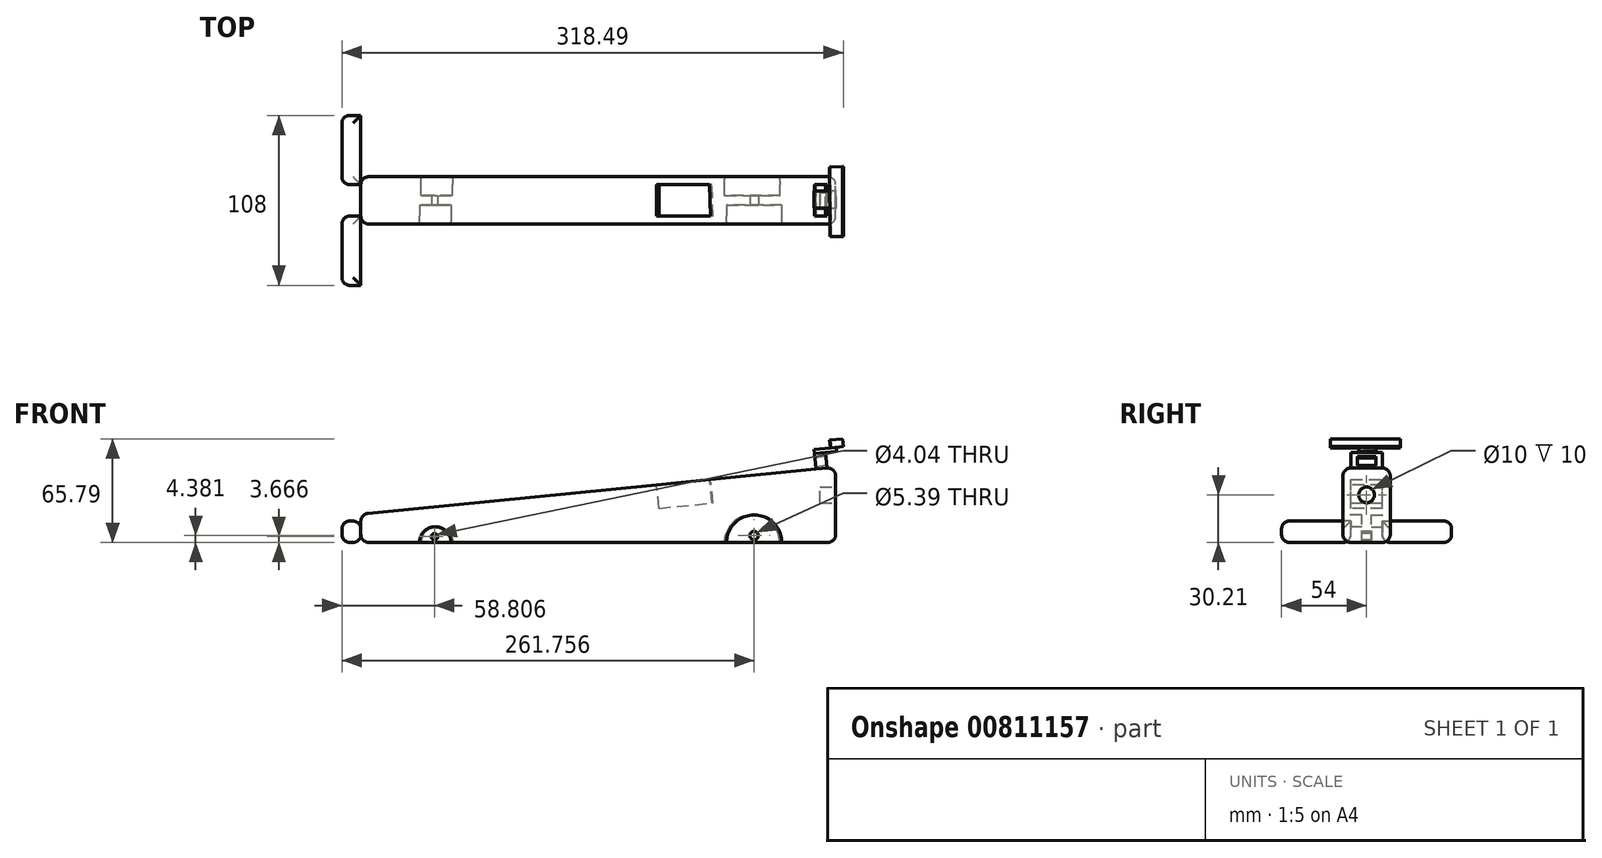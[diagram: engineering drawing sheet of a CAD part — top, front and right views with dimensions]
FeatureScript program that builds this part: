
annotation { "Feature Type Name" : "Feature", "Feature Type Description" : "" }
export const myFeature = defineFeature(function(context is Context, id is Id, definition is map)
    precondition{}
    {
        {
            var Q0;
            Q0=qCreatedBy(makeId("Front.planeOp"),FACE);
            var sketch = newSketch(context, id + "F0", { "sketchPlane" : qUnion([Q0])});
            skLineSegment(sketch, "E0", {"start": v(-158.15, -36.12) * mm, "end": v(143.47, -36.12) * mm});
            skLineSegment(sketch, "E1", {"start": v(143.47, -36.12) * mm, "end": v(143.47, 11.66) * mm});
            skLineSegment(sketch, "E2", {"start": v(-158.15, -36.12) * mm, "end": v(-158.15, -17.99) * mm});
            skLineSegment(sketch, "E3", {"start": v(-158.15, -17.99) * mm, "end": v(143.47, 11.66) * mm});
            skSolve(sketch);
        }
        {
            var Q0;
            Q0 = qSketchRegion(id + "F0", true);
            extrude(context, id + "F1", {"entities" : qUnion([Q0]), "depth" : 30 * mm, "offsetDistance" : 25 * mm});
        }
        {
            var Q0;
            Q0=makeQuery(id+"F1.opExtrude","CAP_FACE",FACE,{"disambiguationData":[OSD([sQuery(id+"F0.wireOp",EDGE,"E0"),sQuery(id+"F0.wireOp",EDGE,"E1"),sQuery(id+"F0.wireOp",EDGE,"E2"),sQuery(id+"F0.wireOp",EDGE,"E3")])],"isStart":false});
            var sketch = newSketch(context, id + "F2", { "sketchPlane" : qUnion([Q0])});
            skCircle(sketch, "E4", {"center": v(-110.88, -36.12) * mm, "radius": 10 * mm});
            skCircle(sketch, "E5", {"center": v(91.67, -36.12) * mm, "radius": 17.5 * mm});
            skSolve(sketch);
        }
        {
            var Q0;
            Q0 = qSketchRegion(id + "F2", true);
            extrude(context, id + "F3", {"entities" : qUnion([Q0]), "operationType" : NewBodyOperationType.REMOVE, "oppositeDirection" : true, "depth" : 12 * mm, "offsetDistance" : 25 * mm});
        }
        {
            var Q0;
            Q0=makeQuery(id+"F1.opExtrude","CAP_FACE",FACE,{"disambiguationData":[OSD([sQuery(id+"F0.wireOp",EDGE,"E0"),sQuery(id+"F0.wireOp",EDGE,"E1"),sQuery(id+"F0.wireOp",EDGE,"E2"),sQuery(id+"F0.wireOp",EDGE,"E3")])],"isStart":true});
            var sketch = newSketch(context, id + "F4", { "sketchPlane" : qUnion([Q0])});
            skCircle(sketch, "E6", {"center": v(109.85, -36.12) * mm, "radius": 10 * mm});
            skCircle(sketch, "E7", {"center": v(-90.42, -36.12) * mm, "radius": 17.5 * mm});
            skSolve(sketch);
        }
        {
            var Q0;
            Q0 = qSketchRegion(id + "F4", true);
            extrude(context, id + "F5", {"entities" : qUnion([Q0]), "operationType" : NewBodyOperationType.REMOVE, "oppositeDirection" : true, "depth" : 12 * mm, "offsetDistance" : 25 * mm});
        }
        {
            var Q0;
            Q0=makeQuery(id+"F1.opExtrude","SWEPT_EDGE",EDGE,{"disambiguationData":[OSD([sQuery(id+"F0.wireOp",EDGE,"E2"),sQuery(id+"F0.wireOp",EDGE,"E3")])]});
            var Q1;
            Q1=makeQuery(id+"F1.opExtrude","CAP_EDGE",EDGE,{"disambiguationData":[OSD([sQuery(id+"F0.wireOp",EDGE,"E3")])],"isStart":false});
            var Q2;
            Q2=makeQuery(id+"F3.boolean.opBoolean","COPY",EDGE,{"derivedFrom":makeQuery(id+"F3.opExtrude","CAP_EDGE",EDGE,{"disambiguationData":[OSD([sQuery(id+"F2.wireOp",EDGE,"E4")])],"isStart":true})});
            var Q3;
            Q3=makeQuery(id+"F1.opExtrude","CAP_EDGE",EDGE,{"disambiguationData":[OSD([sQuery(id+"F0.wireOp",EDGE,"E2")])],"isStart":false});
            var Q4;
            Q4=makeQuery(id+"F3.boolean.opBoolean","COPY",EDGE,{"derivedFrom":makeQuery(id+"F3.opExtrude","CAP_EDGE",EDGE,{"disambiguationData":[OSD([sQuery(id+"F2.wireOp",EDGE,"E5")])],"isStart":true})});
            var Q5;
            Q5=makeQuery(id+"F1.opExtrude","CAP_EDGE",EDGE,{"disambiguationData":[OSD([sQuery(id+"F0.wireOp",EDGE,"E2")])],"isStart":true});
            var Q6;
            Q6=makeQuery(id+"F5.boolean.opBoolean","COPY",EDGE,{"derivedFrom":makeQuery(id+"F5.opExtrude","CAP_EDGE",EDGE,{"disambiguationData":[OSD([sQuery(id+"F4.wireOp",EDGE,"E6")])],"isStart":true})});
            var Q7;
            Q7=makeQuery(id+"F5.boolean.opBoolean","COPY",EDGE,{"derivedFrom":makeQuery(id+"F5.opExtrude","CAP_EDGE",EDGE,{"disambiguationData":[OSD([sQuery(id+"F4.wireOp",EDGE,"E7")])],"isStart":true})});
            var Q8;
            Q8=makeQuery(id+"F1.opExtrude","CAP_EDGE",EDGE,{"disambiguationData":[OSD([sQuery(id+"F0.wireOp",EDGE,"E3")])],"isStart":true});
            var Q9;
            Q9=makeQuery(id+"F1.opExtrude","CAP_EDGE",EDGE,{"disambiguationData":[OSD([sQuery(id+"F0.wireOp",EDGE,"E1")])],"isStart":true});
            var Q10;
            Q10=makeQuery(id+"F1.opExtrude","CAP_EDGE",EDGE,{"disambiguationData":[OSD([sQuery(id+"F0.wireOp",EDGE,"E1")])],"isStart":false});
            var Q11;
            Q11=makeQuery(id+"F1.opExtrude","SWEPT_EDGE",EDGE,{"disambiguationData":[OSD([sQuery(id+"F0.wireOp",EDGE,"E1"),sQuery(id+"F0.wireOp",EDGE,"E3")])]});
            var Q12;
            {var subQ0=sQuery(id+"F0.wireOp",EDGE,"E0");Q12=makeQuery(id+"F5.boolean.opBoolean","SPLIT",EDGE,{"disambiguationData":[TD([makeQuery(id+"F1.opExtrude","SWEPT_FACE",FACE,{"disambiguationData":[OSD([subQ0])]}),makeQuery(id+"F1.opExtrude","CAP_FACE",FACE,{"disambiguationData":[OSD([subQ0,sQuery(id+"F0.wireOp",EDGE,"E1"),sQuery(id+"F0.wireOp",EDGE,"E2"),sQuery(id+"F0.wireOp",EDGE,"E3")])],"isStart":true}),makeQuery(id+"F5.opExtrude","SWEPT_FACE",FACE,{"disambiguationData":[OSD([sQuery(id+"F4.wireOp",EDGE,"E6")])]}),makeQuery(id+"F5.opExtrude","SWEPT_FACE",FACE,{"disambiguationData":[OSD([sQuery(id+"F4.wireOp",EDGE,"E7")])]})])],"derivedFrom":makeQuery(id+"F1.opExtrude","CAP_EDGE",EDGE,{"disambiguationData":[OSD([subQ0])],"isStart":true})});}
            var Q13;
            {var subQ0=sQuery(id+"F0.wireOp",EDGE,"E0");Q13=makeQuery(id+"F3.boolean.opBoolean","SPLIT",EDGE,{"disambiguationData":[TD([makeQuery(id+"F1.opExtrude","SWEPT_FACE",FACE,{"disambiguationData":[OSD([subQ0])]}),makeQuery(id+"F1.opExtrude","CAP_FACE",FACE,{"disambiguationData":[OSD([subQ0,sQuery(id+"F0.wireOp",EDGE,"E1"),sQuery(id+"F0.wireOp",EDGE,"E2"),sQuery(id+"F0.wireOp",EDGE,"E3")])],"isStart":false}),makeQuery(id+"F3.opExtrude","SWEPT_FACE",FACE,{"disambiguationData":[OSD([sQuery(id+"F2.wireOp",EDGE,"E4")])]}),makeQuery(id+"F3.opExtrude","SWEPT_FACE",FACE,{"disambiguationData":[OSD([sQuery(id+"F2.wireOp",EDGE,"E5")])]})])],"derivedFrom":makeQuery(id+"F1.opExtrude","CAP_EDGE",EDGE,{"disambiguationData":[OSD([subQ0])],"isStart":false})});}
            var Q14;
            {var subQ0=sQuery(id+"F0.wireOp",EDGE,"E0");var subQ1=sQuery(id+"F0.wireOp",EDGE,"E1");Q14=makeQuery(id+"F3.boolean.opBoolean","SPLIT",EDGE,{"disambiguationData":[TD([makeQuery(id+"F1.opExtrude","SWEPT_FACE",FACE,{"disambiguationData":[OSD([subQ0])]}),makeQuery(id+"F1.opExtrude","CAP_FACE",FACE,{"disambiguationData":[OSD([subQ0,subQ1,sQuery(id+"F0.wireOp",EDGE,"E2"),sQuery(id+"F0.wireOp",EDGE,"E3")])],"isStart":false}),makeQuery(id+"F1.opExtrude","SWEPT_FACE",FACE,{"disambiguationData":[OSD([subQ1])]}),makeQuery(id+"F3.opExtrude","SWEPT_FACE",FACE,{"disambiguationData":[OSD([sQuery(id+"F2.wireOp",EDGE,"E5")])]})])],"derivedFrom":makeQuery(id+"F1.opExtrude","CAP_EDGE",EDGE,{"disambiguationData":[OSD([subQ0])],"isStart":false})});}
            var Q15;
            {var subQ0=sQuery(id+"F0.wireOp",EDGE,"E0");var subQ1=sQuery(id+"F0.wireOp",EDGE,"E1");Q15=makeQuery(id+"F5.boolean.opBoolean","SPLIT",EDGE,{"disambiguationData":[TD([makeQuery(id+"F1.opExtrude","SWEPT_FACE",FACE,{"disambiguationData":[OSD([subQ0])]}),makeQuery(id+"F1.opExtrude","CAP_FACE",FACE,{"disambiguationData":[OSD([subQ0,subQ1,sQuery(id+"F0.wireOp",EDGE,"E2"),sQuery(id+"F0.wireOp",EDGE,"E3")])],"isStart":true}),makeQuery(id+"F1.opExtrude","SWEPT_FACE",FACE,{"disambiguationData":[OSD([subQ1])]}),makeQuery(id+"F5.opExtrude","SWEPT_FACE",FACE,{"disambiguationData":[OSD([sQuery(id+"F4.wireOp",EDGE,"E7")])]})])],"derivedFrom":makeQuery(id+"F1.opExtrude","CAP_EDGE",EDGE,{"disambiguationData":[OSD([subQ0])],"isStart":true})});}
            var Q16;
            {var subQ0=sQuery(id+"F0.wireOp",EDGE,"E0");var subQ1=sQuery(id+"F0.wireOp",EDGE,"E2");Q16=makeQuery(id+"F5.boolean.opBoolean","SPLIT",EDGE,{"disambiguationData":[TD([makeQuery(id+"F1.opExtrude","SWEPT_FACE",FACE,{"disambiguationData":[OSD([subQ0])]}),makeQuery(id+"F1.opExtrude","CAP_FACE",FACE,{"disambiguationData":[OSD([subQ0,sQuery(id+"F0.wireOp",EDGE,"E1"),subQ1,sQuery(id+"F0.wireOp",EDGE,"E3")])],"isStart":true}),makeQuery(id+"F1.opExtrude","SWEPT_FACE",FACE,{"disambiguationData":[OSD([subQ1])]}),makeQuery(id+"F5.opExtrude","SWEPT_FACE",FACE,{"disambiguationData":[OSD([sQuery(id+"F4.wireOp",EDGE,"E6")])]})])],"derivedFrom":makeQuery(id+"F1.opExtrude","CAP_EDGE",EDGE,{"disambiguationData":[OSD([subQ0])],"isStart":true})});}
            var Q17;
            {var subQ0=sQuery(id+"F0.wireOp",EDGE,"E0");var subQ1=sQuery(id+"F0.wireOp",EDGE,"E2");Q17=makeQuery(id+"F3.boolean.opBoolean","SPLIT",EDGE,{"disambiguationData":[TD([makeQuery(id+"F1.opExtrude","SWEPT_FACE",FACE,{"disambiguationData":[OSD([subQ0])]}),makeQuery(id+"F1.opExtrude","CAP_FACE",FACE,{"disambiguationData":[OSD([subQ0,sQuery(id+"F0.wireOp",EDGE,"E1"),subQ1,sQuery(id+"F0.wireOp",EDGE,"E3")])],"isStart":false}),makeQuery(id+"F1.opExtrude","SWEPT_FACE",FACE,{"disambiguationData":[OSD([subQ1])]}),makeQuery(id+"F3.opExtrude","SWEPT_FACE",FACE,{"disambiguationData":[OSD([sQuery(id+"F2.wireOp",EDGE,"E4")])]})])],"derivedFrom":makeQuery(id+"F1.opExtrude","CAP_EDGE",EDGE,{"disambiguationData":[OSD([subQ0])],"isStart":false})});}
            var Q18;
            Q18=makeQuery(id+"F1.opExtrude","SWEPT_EDGE",EDGE,{"disambiguationData":[OSD([sQuery(id+"F0.wireOp",EDGE,"E0"),sQuery(id+"F0.wireOp",EDGE,"E1")])]});
            fillet(context, id + "F6", {"entities" : qUnion([Q0, Q1, Q2, Q3, Q4, Q5, Q6, Q7, Q8, Q9, Q10, Q11, Q12, Q13, Q14, Q15, Q16, Q17, Q18]), "radius" : 5 * mm, "tangentPropagation" : true, "allowEdgeOverflow" : false});
        }
        {
            var Q0;
            Q0=makeQuery(id+"F1.opExtrude","SWEPT_FACE",FACE,{"disambiguationData":[OSD([sQuery(id+"F0.wireOp",EDGE,"E3")])]});
            var sketch = newSketch(context, id + "F7", { "sketchPlane" : qUnion([Q0])});
            skLineSegment(sketch, "E8", {"start": v(131.22, -5) * mm, "end": v(131.22, -25) * mm});
            skLineSegment(sketch, "E9", {"start": v(131.22, -25) * mm, "end": v(138.4, -25) * mm});
            skLineSegment(sketch, "E10", {"start": v(138.4, -25) * mm, "end": v(138.4, -5) * mm});
            skLineSegment(sketch, "E11", {"start": v(138.4, -5) * mm, "end": v(131.22, -5) * mm});
            skSolve(sketch);
        }
        {
            var Q0;
            Q0 = qSketchRegion(id + "F7", true);
            extrude(context, id + "F8", {"entities" : qUnion([Q0]), "operationType" : NewBodyOperationType.ADD, "depth" : 10 * mm, "offsetDistance" : 25 * mm});
        }
        {
            var Q0;
            Q0=makeQuery(id+"F8.opExtrude","CAP_FACE",FACE,{"disambiguationData":[OSD([sQuery(id+"F7.wireOp",EDGE,"E8"),sQuery(id+"F7.wireOp",EDGE,"E9"),sQuery(id+"F7.wireOp",EDGE,"E10"),sQuery(id+"F7.wireOp",EDGE,"E11")])],"isStart":false});
            var sketch = newSketch(context, id + "F9", { "sketchPlane" : qUnion([Q0])});
            skLineSegment(sketch, "E12", {"start": v(131.22, -9.22) * mm, "end": v(131.22, -20) * mm});
            skLineSegment(sketch, "E13", {"start": v(131.22, -20) * mm, "end": v(145.56, -20) * mm});
            skLineSegment(sketch, "E14", {"start": v(145.56, -20) * mm, "end": v(145.56, -9.13) * mm});
            skLineSegment(sketch, "E15", {"start": v(145.56, -9.13) * mm, "end": v(131.22, -9.22) * mm});
            skSolve(sketch);
        }
        {
            var Q0;
            Q0 = qSketchRegion(id + "F9", true);
            extrude(context, id + "F10", {"entities" : qUnion([Q0]), "operationType" : NewBodyOperationType.ADD, "depth" : 2.5 * mm, "offsetDistance" : 25 * mm});
        }
        {
            var Q0;
            Q0=makeQuery(id+"F10.opExtrude","CAP_FACE",FACE,{"disambiguationData":[OSD([sQuery(id+"F9.wireOp",EDGE,"E12"),sQuery(id+"F9.wireOp",EDGE,"E13"),sQuery(id+"F9.wireOp",EDGE,"E14"),sQuery(id+"F9.wireOp",EDGE,"E15")])],"isStart":false});
            var sketch = newSketch(context, id + "F11", { "sketchPlane" : qUnion([Q0])});
            skLineSegment(sketch, "E16", {"start": v(141.8, 6.32) * mm, "end": v(142.05, -37.95) * mm});
            skPoint(sketch, "E17.start.orphan", {"position": v(151.86, 7.12) * mm});
            skLineSegment(sketch, "E18", {"start": v(141.8, 6.32) * mm, "end": v(150.04, 6.37) * mm});
            skLineSegment(sketch, "E19", {"start": v(150.04, 6.37) * mm, "end": v(150.04, -37.9) * mm});
            skPoint(sketch, "E20.end.orphan", {"position": v(151.86, -37.9) * mm});
            skLineSegment(sketch, "E21", {"start": v(142.05, -37.95) * mm, "end": v(150.04, -37.9) * mm});
            skSolve(sketch);
        }
        {
            var Q0;
            Q0 = qSketchRegion(id + "F11", true);
            extrude(context, id + "F12", {"entities" : qUnion([Q0]), "operationType" : NewBodyOperationType.ADD, "depth" : 5 * mm, "offsetDistance" : 25 * mm});
        }
        {
            var Q0;
            Q0=makeQuery(id+"F10.boolean.opBoolean","MERGE",FACE,{"derivedFrom":[makeQuery(id+"F8.opExtrude","SWEPT_FACE",FACE,{"disambiguationData":[OSD([sQuery(id+"F7.wireOp",EDGE,"E8")])]}),makeQuery(id+"F10.opExtrude","SWEPT_FACE",FACE,{"disambiguationData":[OSD([sQuery(id+"F9.wireOp",EDGE,"E12")])]})]});
            var sketch = newSketch(context, id + "F13", { "sketchPlane" : qUnion([Q0])});
            skLineSegment(sketch, "E22.bottom", {"start": v(9.22, 4.84) * mm, "end": v(20.97, 4.84) * mm});
            skLineSegment(sketch, "E22.top", {"start": v(9.22, -0.9) * mm, "end": v(20.97, -0.9) * mm});
            skLineSegment(sketch, "E22.left", {"start": v(9.22, 4.84) * mm, "end": v(9.22, -0.9) * mm});
            skLineSegment(sketch, "E22.right", {"start": v(20.97, 4.84) * mm, "end": v(20.97, -0.9) * mm});
            skSolve(sketch);
        }
        {
            var Q0;
            Q0 = qSketchRegion(id + "F13", true);
            extrude(context, id + "F14", {"entities" : qUnion([Q0]), "operationType" : NewBodyOperationType.REMOVE, "oppositeDirection" : true, "depth" : 25 * mm, "offsetDistance" : 25 * mm});
        }
        {
            var Q0;
            Q0=makeQuery(id+"F3.boolean.opBoolean","COPY",FACE,{"derivedFrom":makeQuery(id+"F3.opExtrude","CAP_FACE",FACE,{"disambiguationData":[OSD([sQuery(id+"F2.wireOp",EDGE,"E4")])],"isStart":false})});
            var sketch = newSketch(context, id + "F15", { "sketchPlane" : qUnion([Q0])});
            skCircle(sketch, "E23", {"center": v(-111.34, -32.45) * mm, "radius": 2.02 * mm});
            skSolve(sketch);
        }
        {
            var Q0;
            Q0 = qSketchRegion(id + "F15", true);
            extrude(context, id + "F16", {"entities" : qUnion([Q0]), "operationType" : NewBodyOperationType.REMOVE, "oppositeDirection" : true, "depth" : 25 * mm, "offsetDistance" : 25 * mm});
        }
        {
            var Q0;
            Q0=makeQuery(id+"F3.boolean.opBoolean","COPY",FACE,{"derivedFrom":makeQuery(id+"F3.opExtrude","CAP_FACE",FACE,{"disambiguationData":[OSD([sQuery(id+"F2.wireOp",EDGE,"E5")])],"isStart":false})});
            var sketch = newSketch(context, id + "F17", { "sketchPlane" : qUnion([Q0])});
            skCircle(sketch, "E24", {"center": v(91.6, -31.74) * mm, "radius": 2.7 * mm});
            skSolve(sketch);
        }
        {
            var Q0;
            Q0 = qSketchRegion(id + "F17", true);
            extrude(context, id + "F18", {"entities" : qUnion([Q0]), "operationType" : NewBodyOperationType.REMOVE, "oppositeDirection" : true, "depth" : 25 * mm, "offsetDistance" : 25 * mm});
        }
        {
            var Q0;
            Q0=makeQuery(id+"F1.opExtrude","SWEPT_FACE",FACE,{"disambiguationData":[OSD([sQuery(id+"F0.wireOp",EDGE,"E2")])]});
            var sketch = newSketch(context, id + "F19", { "sketchPlane" : qUnion([Q0])});
            skLineSegment(sketch, "E25", {"start": v(5, -22.52) * mm, "end": v(-39, -22.52) * mm});
            skLineSegment(sketch, "E26", {"start": v(-39, -22.52) * mm, "end": v(-39, -36.12) * mm});
            skLineSegment(sketch, "E27", {"start": v(-39, -36.12) * mm, "end": v(5, -36.12) * mm});
            skLineSegment(sketch, "E28", {"start": v(5, -36.12) * mm, "end": v(5, -22.52) * mm});
            skLineSegment(sketch, "E29", {"start": v(25, -22.52) * mm, "end": v(69, -22.52) * mm});
            skLineSegment(sketch, "E30", {"start": v(69, -22.52) * mm, "end": v(69, -36.12) * mm});
            skLineSegment(sketch, "E31", {"start": v(69, -36.12) * mm, "end": v(25, -36.12) * mm});
            skLineSegment(sketch, "E32", {"start": v(25, -36.12) * mm, "end": v(25, -22.52) * mm});
            skSolve(sketch);
        }
        {
            var Q0;
            Q0 = qSketchRegion(id + "F19", true);
            extrude(context, id + "F20", {"entities" : qUnion([Q0]), "depth" : 12 * mm, "offsetDistance" : 25 * mm});
        }
        {
            var Q0;
            Q0=makeQuery(id+"F20.opExtrude","CAP_EDGE",EDGE,{"disambiguationData":[OSD([sQuery(id+"F19.wireOp",EDGE,"E25")])],"isStart":false});
            var Q1;
            Q1=makeQuery(id+"F20.opExtrude","CAP_EDGE",EDGE,{"disambiguationData":[OSD([sQuery(id+"F19.wireOp",EDGE,"E29")])],"isStart":false});
            var Q2;
            Q2=makeQuery(id+"F20.opExtrude","CAP_EDGE",EDGE,{"disambiguationData":[OSD([sQuery(id+"F19.wireOp",EDGE,"E30")])],"isStart":false});
            var Q3;
            Q3=makeQuery(id+"F20.opExtrude","CAP_EDGE",EDGE,{"disambiguationData":[OSD([sQuery(id+"F19.wireOp",EDGE,"E31")])],"isStart":false});
            var Q4;
            Q4=makeQuery(id+"F20.opExtrude","CAP_EDGE",EDGE,{"disambiguationData":[OSD([sQuery(id+"F19.wireOp",EDGE,"E27")])],"isStart":false});
            var Q5;
            Q5=makeQuery(id+"F20.opExtrude","CAP_EDGE",EDGE,{"disambiguationData":[OSD([sQuery(id+"F19.wireOp",EDGE,"E26")])],"isStart":false});
            var Q6;
            Q6=makeQuery(id+"F20.opExtrude","SWEPT_EDGE",EDGE,{"disambiguationData":[OSD([sQuery(id+"F19.wireOp",EDGE,"E30"),sQuery(id+"F19.wireOp",EDGE,"E31")])]});
            var Q7;
            Q7=makeQuery(id+"F20.opExtrude","SWEPT_EDGE",EDGE,{"disambiguationData":[OSD([sQuery(id+"F19.wireOp",EDGE,"E29"),sQuery(id+"F19.wireOp",EDGE,"E30")])]});
            var Q8;
            Q8=makeQuery(id+"F20.opExtrude","CAP_EDGE",EDGE,{"disambiguationData":[OSD([sQuery(id+"F19.wireOp",EDGE,"E28")])],"isStart":false});
            var Q9;
            Q9=makeQuery(id+"F20.opExtrude","CAP_EDGE",EDGE,{"disambiguationData":[OSD([sQuery(id+"F19.wireOp",EDGE,"E32")])],"isStart":false});
            var Q10;
            Q10=makeQuery(id+"F20.opExtrude","SWEPT_EDGE",EDGE,{"disambiguationData":[OSD([sQuery(id+"F19.wireOp",EDGE,"E25"),sQuery(id+"F19.wireOp",EDGE,"E26")])]});
            var Q11;
            Q11=makeQuery(id+"F20.opExtrude","SWEPT_EDGE",EDGE,{"disambiguationData":[OSD([sQuery(id+"F19.wireOp",EDGE,"E26"),sQuery(id+"F19.wireOp",EDGE,"E27")])]});
            var Q12;
            Q12=makeQuery(id+"F20.opExtrude","CAP_EDGE",EDGE,{"disambiguationData":[OSD([sQuery(id+"F19.wireOp",EDGE,"E31")])],"isStart":true});
            var Q13;
            Q13=makeQuery(id+"F20.opExtrude","CAP_EDGE",EDGE,{"disambiguationData":[OSD([sQuery(id+"F19.wireOp",EDGE,"E27")])],"isStart":true});
            var Q14;
            Q14=makeQuery(id+"F20.opExtrude","SWEPT_EDGE",EDGE,{"disambiguationData":[OSD([sQuery(id+"F0.wireOp",EDGE,"E0"),sQuery(id+"F0.wireOp",EDGE,"E2"),sQuery(id+"F19.wireOp",EDGE,"E27"),sQuery(id+"F19.wireOp",EDGE,"E28")])]});
            var Q15;
            Q15=makeQuery(id+"F20.opExtrude","SWEPT_EDGE",EDGE,{"disambiguationData":[OSD([sQuery(id+"F0.wireOp",EDGE,"E0"),sQuery(id+"F0.wireOp",EDGE,"E2"),sQuery(id+"F19.wireOp",EDGE,"E31"),sQuery(id+"F19.wireOp",EDGE,"E32")])]});
            var Q16;
            Q16=makeQuery(id+"F1.opExtrude","SWEPT_EDGE",EDGE,{"disambiguationData":[OSD([sQuery(id+"F0.wireOp",EDGE,"E0"),sQuery(id+"F0.wireOp",EDGE,"E2")])]});
            var Q17;
            Q17=makeQuery(id+"F20.opExtrude","CAP_EDGE",EDGE,{"disambiguationData":[OSD([sQuery(id+"F19.wireOp",EDGE,"E29")])],"isStart":true});
            var Q18;
            Q18=makeQuery(id+"F20.opExtrude","CAP_EDGE",EDGE,{"disambiguationData":[OSD([sQuery(id+"F19.wireOp",EDGE,"E25")])],"isStart":true});
            fillet(context, id + "F21", {"entities" : qUnion([Q0, Q1, Q2, Q3, Q4, Q5, Q6, Q7, Q8, Q9, Q10, Q11, Q12, Q13, Q14, Q15, Q16, Q17, Q18]), "radius" : 5 * mm, "tangentPropagation" : true, "allowEdgeOverflow" : false});
        }
        {
            var Q0;
            Q0=makeQuery(id+"F1.opExtrude","SWEPT_FACE",FACE,{"disambiguationData":[OSD([sQuery(id+"F0.wireOp",EDGE,"E3")])]});
            var sketch = newSketch(context, id + "F22", { "sketchPlane" : qUnion([Q0])});
            skLineSegment(sketch, "E33", {"start": v(63.52, -5) * mm, "end": v(29.65, -5) * mm});
            skLineSegment(sketch, "E34", {"start": v(29.65, -5) * mm, "end": v(29.65, -25) * mm});
            skLineSegment(sketch, "E35", {"start": v(29.65, -25) * mm, "end": v(64.1, -25) * mm});
            skLineSegment(sketch, "E36", {"start": v(64.1, -25) * mm, "end": v(63.52, -5) * mm});
            skSolve(sketch);
        }
        {
            var Q0;
            Q0 = qSketchRegion(id + "F22", true);
            extrude(context, id + "F23", {"entities" : qUnion([Q0]), "operationType" : NewBodyOperationType.REMOVE, "oppositeDirection" : true, "depth" : 15 * mm, "offsetDistance" : 25 * mm});
        }
        {
            var Q0;
            Q0=makeQuery(id+"F1.opExtrude","SWEPT_FACE",FACE,{"disambiguationData":[OSD([sQuery(id+"F0.wireOp",EDGE,"E1")])]});
            var sketch = newSketch(context, id + "F24", { "sketchPlane" : qUnion([Q0])});
            skCircle(sketch, "E37", {"center": v(-15, -5.9) * mm, "radius": 5 * mm});
            skPoint(sketch, "E37.centerSnap0", {"position": v(-15, 6.14) * mm});
            skSolve(sketch);
        }
        {
            var Q0;
            Q0 = qSketchRegion(id + "F24", true);
            extrude(context, id + "F25", {"entities" : qUnion([Q0]), "operationType" : NewBodyOperationType.REMOVE, "oppositeDirection" : true, "depth" : 10 * mm, "offsetDistance" : 25 * mm});
        }
    });
